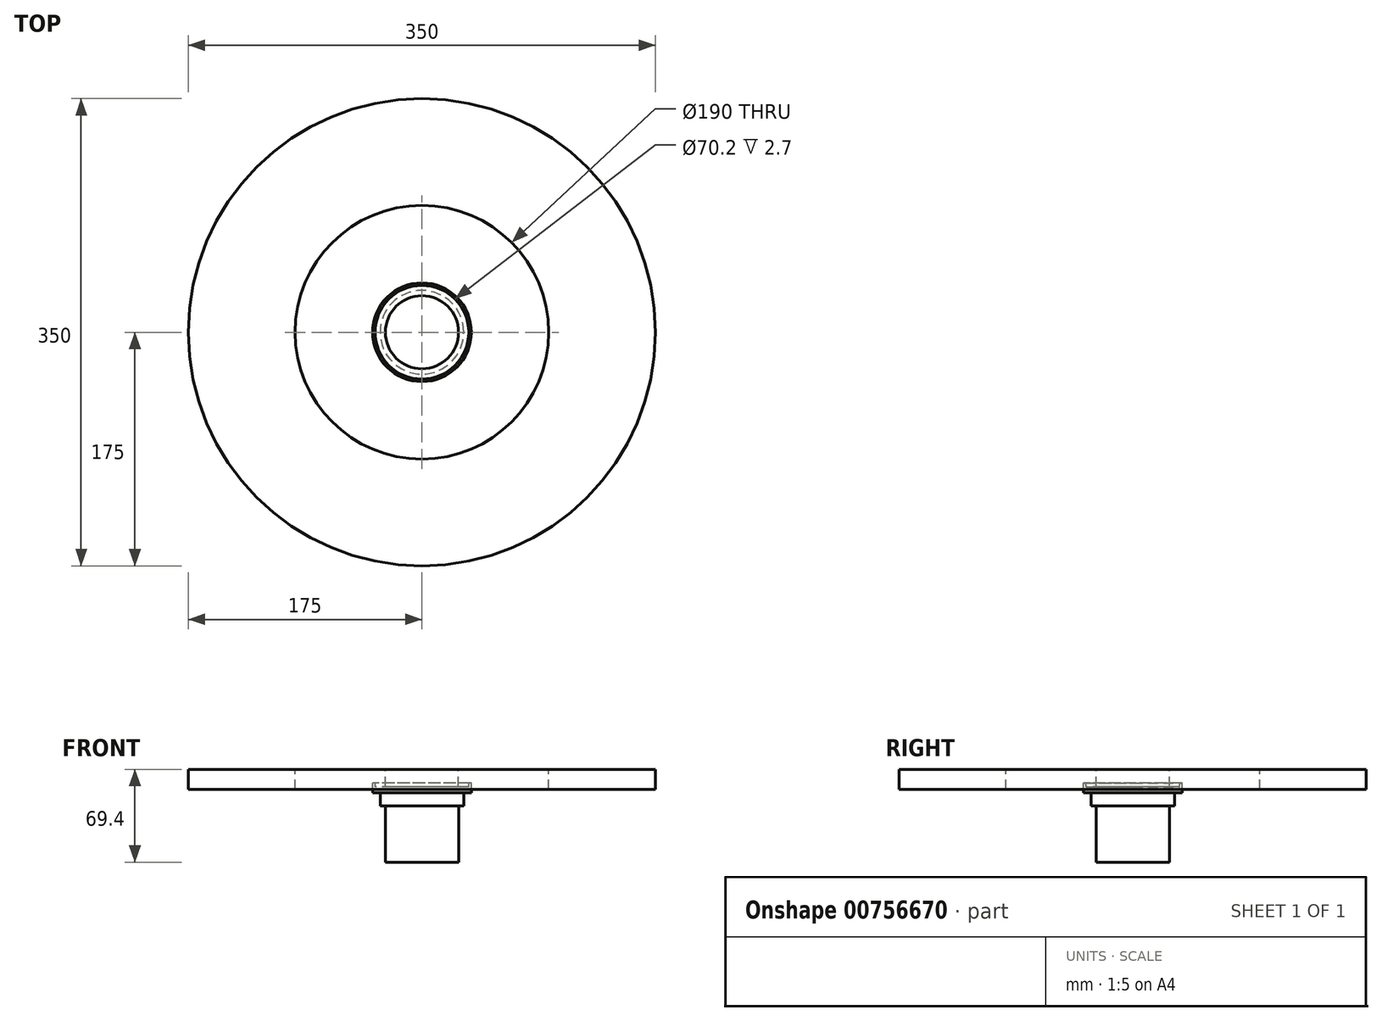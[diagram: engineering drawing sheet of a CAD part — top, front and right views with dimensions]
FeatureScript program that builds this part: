
annotation { "Feature Type Name" : "Feature", "Feature Type Description" : "" }
export const myFeature = defineFeature(function(context is Context, id is Id, definition is map)
    precondition{}
    {
        {
            var Q0;
            Q0=qCreatedBy(makeId("Front.planeOp"),FACE);
            var sketch = newSketch(context, id + "F0", { "sketchPlane" : qUnion([Q0])});
            skLineSegment(sketch, "E0", {"start": v(0, 0) * mm, "end": v(27.4, 0) * mm});
            skLineSegment(sketch, "E1", {"start": v(27.4, 0) * mm, "end": v(27.4, -12.9) * mm});
            skLineSegment(sketch, "E2", {"start": v(27.4, -12.9) * mm, "end": v(35.1, -12.9) * mm});
            skLineSegment(sketch, "E3", {"start": v(35.1, -12.9) * mm, "end": v(35.1, -10.2) * mm});
            skLineSegment(sketch, "E4", {"start": v(35.1, -10.2) * mm, "end": v(37, -10.2) * mm});
            skLineSegment(sketch, "E5", {"start": v(37, -10.2) * mm, "end": v(37, -17.4) * mm});
            skLineSegment(sketch, "E6", {"start": v(37, -17.4) * mm, "end": v(31.3, -17.4) * mm});
            skLineSegment(sketch, "E7", {"start": v(31.3, -17.4) * mm, "end": v(31.3, -27.4) * mm});
            skLineSegment(sketch, "E8", {"start": v(31.3, -27.4) * mm, "end": v(27.5, -27.4) * mm});
            skLineSegment(sketch, "E9", {"start": v(27.5, -27.4) * mm, "end": v(27.5, -69.4) * mm});
            skLineSegment(sketch, "E10", {"start": v(0, 59.19) * mm, "end": v(0, -76.7) * mm, "construction": true});
            skLineSegment(sketch, "E11", {"start": v(0, 0) * mm, "end": v(0, -69.4) * mm});
            skLineSegment(sketch, "E12", {"start": v(0, -69.4) * mm, "end": v(27.5, -69.4) * mm});
            skSolve(sketch);
        }
        {
            var Q0;
            Q0 = qSketchRegion(id + "F0", true);
            var Q1;
            Q1=sQuery(id+"F0.wireOp",EDGE,"E11");
            revolve(context, id + "F1", {"surfaceOperationType" : NewSurfaceOperationType.NEW, "entities" : qUnion([Q0]), "axis" : qUnion([Q1]), "revolveType" : RevolveType.FULL});
        }
        {
            var Q0;
            Q0=qCreatedBy(makeId("Top.planeOp"),FACE);
            var sketch = newSketch(context, id + "F2", { "sketchPlane" : qUnion([Q0])});
            skCircle(sketch, "E13", {"center": v(0, 0) * mm, "radius": 95 * mm});
            skCircle(sketch, "E14", {"center": v(0, 0) * mm, "radius": 175 * mm});
            skSolve(sketch);
        }
        {
            var Q0;
            Q0 = qSketchRegion(id + "F2", true);
            var Q1;
            Q1=makeQuery(id+"F2.imprint","IMPRINT",FACE,{"disambiguationData":[TD([[makeQuery(id+"F2.imprint","IMPRINT",EDGE,{"derivedFrom":sQuery(id+"F2.wireOp",EDGE,"E13")}),-1.0]])]});
            extrude(context, id + "F3", {"entities" : qUnion([Q0, Q1]), "oppositeDirection" : true, "depth" : 15 * mm, "offsetDistance" : 25 * mm});
        }
    });
